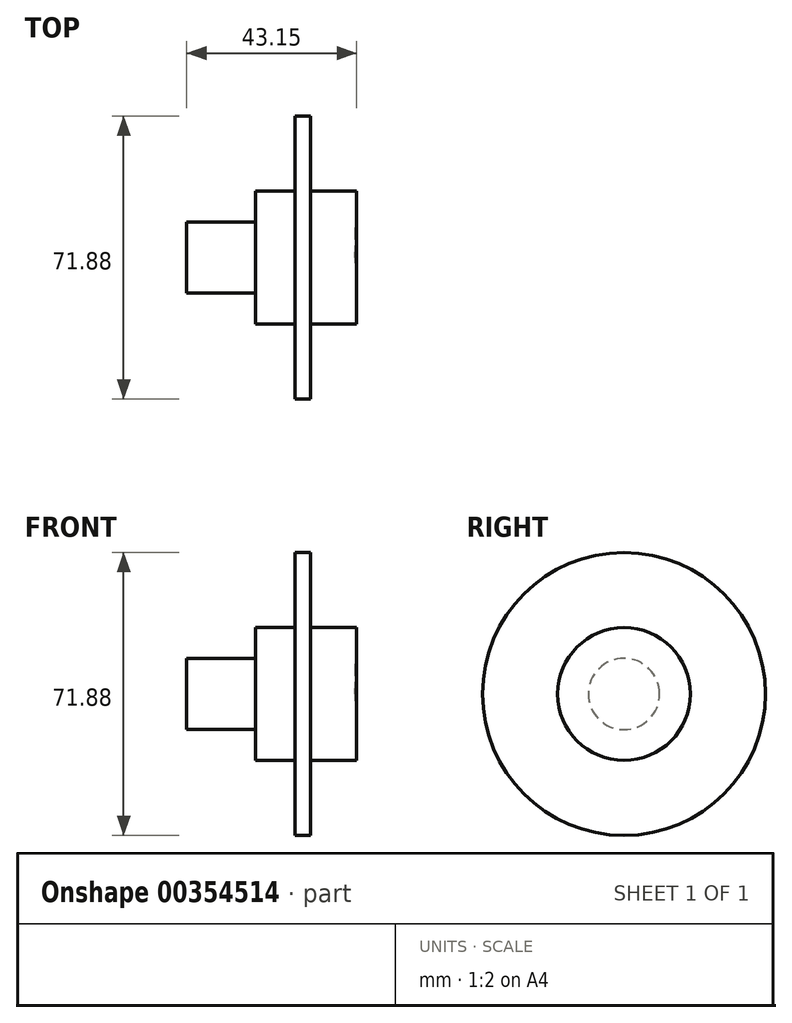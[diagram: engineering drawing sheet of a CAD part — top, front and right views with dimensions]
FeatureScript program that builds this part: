
annotation { "Feature Type Name" : "Feature", "Feature Type Description" : "" }
export const myFeature = defineFeature(function(context is Context, id is Id, definition is map)
    precondition{}
    {
        {
            var Q0;
            Q0=qCreatedBy(makeId("Front.planeOp"),FACE);
            var sketch = newSketch(context, id + "F0", { "sketchPlane" : qUnion([Q0])});
            skLineSegment(sketch, "E0", {"start": v(0, 0) * mm, "end": v(-42.77, 0) * mm});
            skLineSegment(sketch, "E1", {"start": v(-42.77, 0) * mm, "end": v(-42.77, 9.04) * mm});
            skLineSegment(sketch, "E2", {"start": v(-42.77, 9.04) * mm, "end": v(-25.24, 9.04) * mm});
            skLineSegment(sketch, "E3", {"start": v(-25.24, 9.04) * mm, "end": v(-25.24, 16.87) * mm});
            skLineSegment(sketch, "E4", {"start": v(-25.24, 16.87) * mm, "end": v(-15.27, 16.87) * mm});
            skLineSegment(sketch, "E5", {"start": v(-15.27, 16.87) * mm, "end": v(-15.27, 35.94) * mm});
            skLineSegment(sketch, "E6", {"start": v(-15.27, 35.94) * mm, "end": v(-11.35, 35.94) * mm});
            skLineSegment(sketch, "E7", {"start": v(-11.35, 35.94) * mm, "end": v(-11.35, 16.87) * mm});
            skLineSegment(sketch, "E8", {"start": v(-11.35, 16.87) * mm, "end": v(0.38, 16.87) * mm});
            skLineSegment(sketch, "E9", {"start": v(0.38, 16.87) * mm, "end": v(0, 0) * mm});
            skSolve(sketch);
        }
        {
            var Q0;
            Q0=makeQuery(id+"F0.imprint","IMPRINT",FACE,{"disambiguationData":[TD([[makeQuery(id+"F0.imprint","IMPRINT",EDGE,{"derivedFrom":sQuery(id+"F0.wireOp",EDGE,"E0")}),-1.0]])]});
            var Q1;
            Q1=sQuery(id+"F0.wireOp",EDGE,"E0");
            revolve(context, id + "F1", {"entities" : qUnion([Q0]), "axis" : qUnion([Q1]), "revolveType" : RevolveType.FULL});
        }
    });
